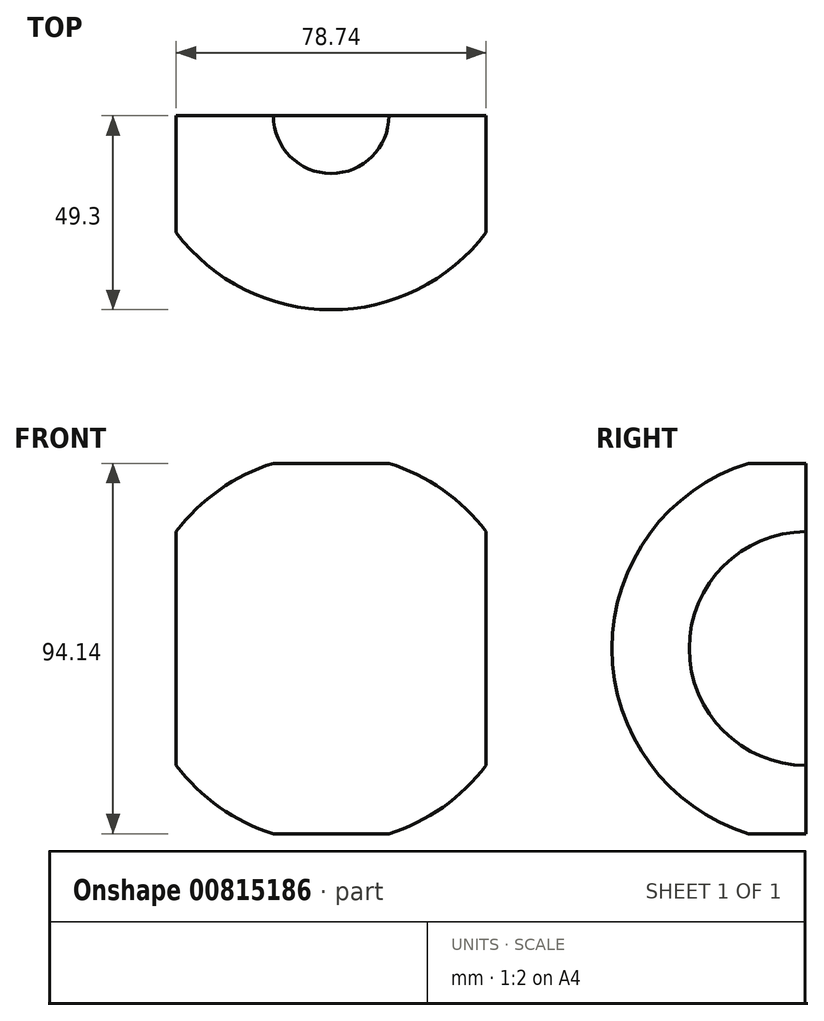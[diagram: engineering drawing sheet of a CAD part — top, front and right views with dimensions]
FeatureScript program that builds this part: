
annotation { "Feature Type Name" : "Feature", "Feature Type Description" : "" }
export const myFeature = defineFeature(function(context is Context, id is Id, definition is map)
    precondition{}
    {
        {
            var Q0;
            Q0=qCreatedBy(makeId("Front.planeOp"),FACE);
            var sketch = newSketch(context, id + "F0", { "sketchPlane" : qUnion([Q0])});
            skLineSegment(sketch, "E0.bottom", {"start": v(39.37, -47.07) * mm, "end": v(-39.37, -47.07) * mm});
            skLineSegment(sketch, "E0.top", {"start": v(39.37, 47.07) * mm, "end": v(-39.37, 47.07) * mm});
            skLineSegment(sketch, "E0.left", {"start": v(39.37, -47.07) * mm, "end": v(39.37, 47.07) * mm});
            skLineSegment(sketch, "E0.right", {"start": v(-39.37, -47.07) * mm, "end": v(-39.37, 47.07) * mm});
            skPoint(sketch, "E0.middle", {"position": v(0, 0) * mm});
            skSolve(sketch);
        }
        {
            var Q0;
            Q0=makeQuery(id+"F0.imprint","IMPRINT",FACE,{"disambiguationData":[TD([[makeQuery(id+"F0.imprint","IMPRINT",EDGE,{"derivedFrom":sQuery(id+"F0.wireOp",EDGE,"E0.bottom")}),-1.0]])]});
            extrude(context, id + "F1", {"entities" : qUnion([Q0]), "depth" : 85.5 * mm, "offsetDistance" : 25 * mm});
        }
        {
            var Q0;
            Q0=qCreatedBy(makeId("Front.planeOp"),FACE);
            var sketch = newSketch(context, id + "F2", { "sketchPlane" : qUnion([Q0])});
            skArc(sketch, "E1", {"start": v(0, 49.3) * mm, "mid": v(-49.3, 0) * mm, "end": v(0, -49.3) * mm});
            skLineSegment(sketch, "E2", {"start": v(0, 0) * mm, "end": v(0, 49.3) * mm});
            skLineSegment(sketch, "E3", {"start": v(0, 49.3) * mm, "end": v(0, -49.3) * mm});
            skSolve(sketch);
        }
        {
            var Q0;
            {var subQ0=sQuery(id+"F2.wireOp",EDGE,"E1");Q0=makeQuery(id+"F2.imprint","IMPRINT",FACE,{"disambiguationData":[TD([[makeQuery(id+"F2.imprint","IMPRINT",EDGE,{"derivedFrom":subQ0}),1.0]])]});}
            var Q1;
            Q1=sQuery(id+"F2.wireOp",EDGE,"E3");
            revolve(context, id + "F3", {"surfaceOperationType" : NewSurfaceOperationType.NEW, "entities" : qUnion([Q0]), "axis" : qUnion([Q1]), "revolveType" : RevolveType.FULL});
        }
        {
            var Q0;
            Q0=makeQuery(id+"F1.opExtrude","SWEPT_BODY",BODY,{"disambiguationData":[OSD([sQuery(id+"F0.wireOp",EDGE,"E0.bottom"),sQuery(id+"F0.wireOp",EDGE,"E0.top"),sQuery(id+"F0.wireOp",EDGE,"E0.left"),sQuery(id+"F0.wireOp",EDGE,"E0.right")])]});
            var Q1;
            Q1=makeQuery(id+"F3.opRevolve","SWEPT_BODY",BODY,{"disambiguationData":[OSD([sQuery(id+"F2.wireOp",EDGE,"E1"),sQuery(id+"F2.wireOp",EDGE,"E3")])]});
            booleanBodies(context, id + "F4", {"operationType" : BooleanOperationType.INTERSECTION, "tools" : qUnion([Q0, Q1])});
        }
    });
